# Revit family: Remote indicator
name_source: partatom
category: Fire Alarm Devices
revit_build: Autodesk Revit 2014 (Build: 20130308_1515(x64)
units: mm (PartAtom-declared; Revit-internal decimal feet)

## types (2) — shared parameters
Manufacturer = Esser by Honeywell
URL = http://www.esser-systems.com
b1 = 27 mm  [stored 0.0885827 ft]
content_date_modified = 16.06.2015
content_version = 1.0
h1 = 82 mm  [stored 0.269029 ft]
l1 = 85 mm  [stored 0.278871 ft]
l2 = 25 mm  [stored 0.082021 ft]
material = White
material 2 = Red

## per-type parameters (varying)
| type | Model | article number |
| Remote indicator esserbus-PLus | Remote indicator esserbus-PLus for detector series 9200 and IQ8Quad, red | 801824 |
| Remote indicator red | Remote indicator for Series 9000, 9200 and IQ8Quad, red | 781814 |

note: [stored X ft] marks values corroborated as IEEE doubles in the binary element streams (Revit-internal decimal feet)

## geometry (parser evidence)
native form markers: Sweep x4
no freeform markers — native parametric forms only
